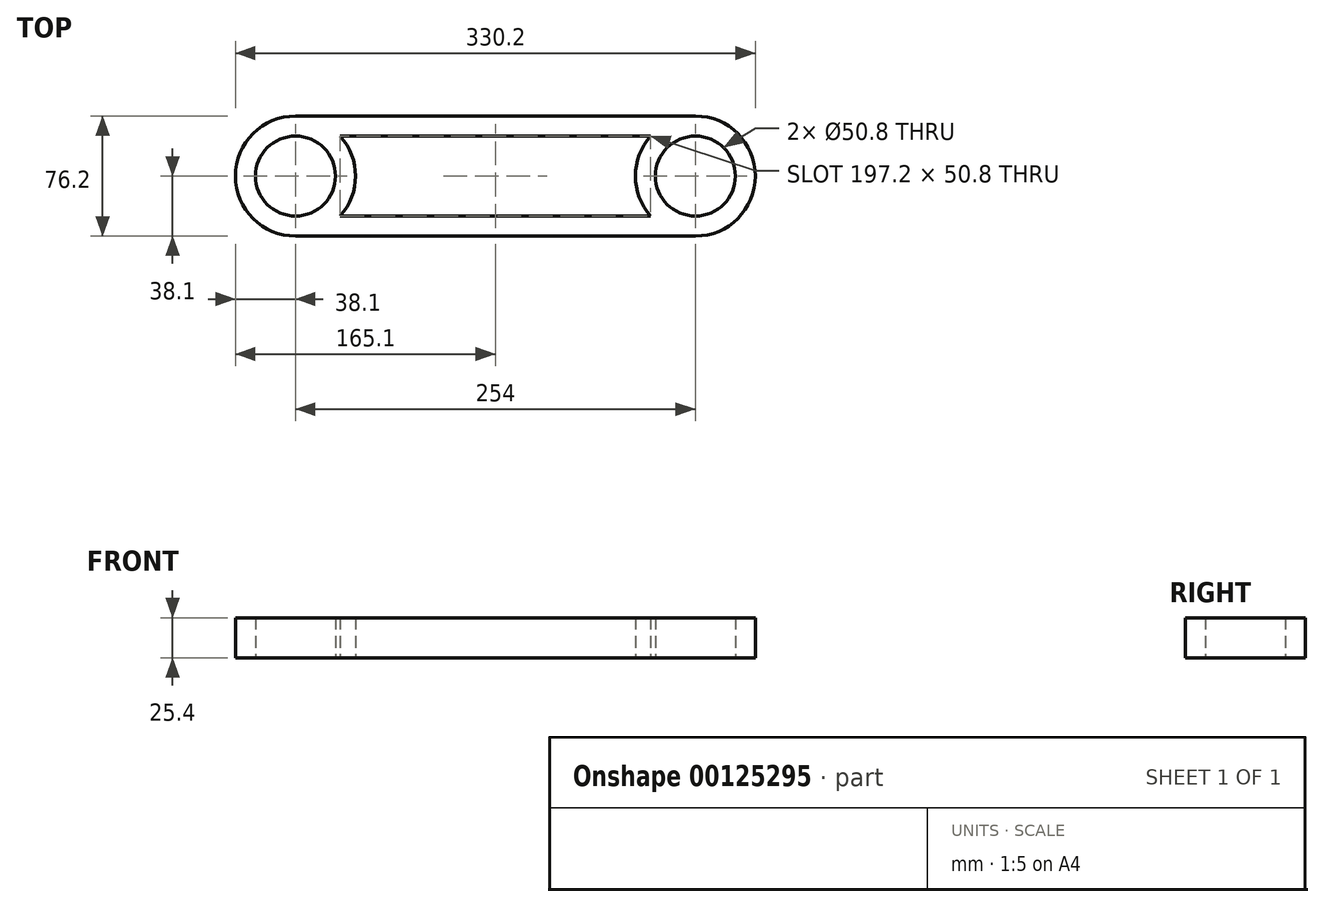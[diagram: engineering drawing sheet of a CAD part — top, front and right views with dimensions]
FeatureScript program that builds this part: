
annotation { "Feature Type Name" : "Feature", "Feature Type Description" : "" }
export const myFeature = defineFeature(function(context is Context, id is Id, definition is map)
    precondition{}
    {
        {
            var Q0;
            Q0=qCreatedBy(makeId("Top.planeOp"),FACE);
            var sketch = newSketch(context, id + "F0", { "sketchPlane" : qUnion([Q0])});
            skCircle(sketch, "E0", {"center": v(0, 0) * mm, "radius": 25.4 * mm});
            skCircle(sketch, "E1", {"center": v(0, 0) * mm, "radius": 38.1 * mm});
            skCircle(sketch, "E2", {"center": v(254, 0) * mm, "radius": 25.4 * mm});
            skCircle(sketch, "E3", {"center": v(254, 0) * mm, "radius": 38.1 * mm});
            skLineSegment(sketch, "E4", {"start": v(0, 38.1) * mm, "end": v(254, 38.1) * mm});
            skLineSegment(sketch, "E5", {"start": v(0, -25.4) * mm, "end": v(254, -25.4) * mm});
            skLineSegment(sketch, "E6", {"start": v(0, 25.4) * mm, "end": v(254, 25.4) * mm});
            skLineSegment(sketch, "E7", {"start": v(0, -38.1) * mm, "end": v(254, -38.1) * mm});
            skSolve(sketch);
        }
        {
            var Q0;
            {var subQ2=sQuery(id+"F0.wireOp",EDGE,"E5");var subQ7=sQuery(id+"F0.wireOp",EDGE,"E0");var subQ8=makeQuery(id+"F0.imprint","INTERSECT",VERTEX,{"derivedFrom":[subQ7,subQ2]});Q0=makeQuery(id+"F0.imprint","IMPRINT",FACE,{"disambiguationData":[TD([[makeQuery(id+"F0.imprint","IMPRINT",EDGE,{"disambiguationData":[TD([[subQ8,1.0]])],"derivedFrom":subQ7}),-1.0]])]});}
            var Q1;
            {var subQ0=sQuery(id+"F0.wireOp",EDGE,"E4");Q1=makeQuery(id+"F0.imprint","IMPRINT",FACE,{"disambiguationData":[TD([[makeQuery(id+"F0.imprint","IMPRINT",EDGE,{"derivedFrom":subQ0}),-1.0]])]});}
            var Q2;
            {var subQ3=sQuery(id+"F0.wireOp",EDGE,"E5");var subQ7=sQuery(id+"F0.wireOp",EDGE,"E2");var subQ8=makeQuery(id+"F0.imprint","INTERSECT",VERTEX,{"derivedFrom":[subQ7,subQ3]});Q2=makeQuery(id+"F0.imprint","IMPRINT",FACE,{"disambiguationData":[TD([[makeQuery(id+"F0.imprint","IMPRINT",EDGE,{"disambiguationData":[TD([[subQ8,-1.0]])],"derivedFrom":subQ7}),-1.0]])]});}
            var Q3;
            {var subQ0=sQuery(id+"F0.wireOp",EDGE,"E7");Q3=makeQuery(id+"F0.imprint","IMPRINT",FACE,{"disambiguationData":[TD([[makeQuery(id+"F0.imprint","IMPRINT",EDGE,{"derivedFrom":subQ0}),1.0]])]});}
            var Q4;
            {var subQ0=sQuery(id+"F0.wireOp",EDGE,"E5");var subQ1=sQuery(id+"F0.wireOp",EDGE,"E0");var subQ2=makeQuery(id+"F0.imprint","INTERSECT",VERTEX,{"derivedFrom":[subQ1,subQ0]});Q4=makeQuery(id+"F0.imprint","IMPRINT",FACE,{"disambiguationData":[TD([[makeQuery(id+"F0.imprint","IMPRINT",EDGE,{"disambiguationData":[TD([[subQ2,-1.0]])],"derivedFrom":subQ1}),-1.0]])]});}
            var Q5;
            {var subQ0=sQuery(id+"F0.wireOp",EDGE,"E5");var subQ1=sQuery(id+"F0.wireOp",EDGE,"E2");var subQ2=makeQuery(id+"F0.imprint","INTERSECT",VERTEX,{"derivedFrom":[subQ1,subQ0]});Q5=makeQuery(id+"F0.imprint","IMPRINT",FACE,{"disambiguationData":[TD([[makeQuery(id+"F0.imprint","IMPRINT",EDGE,{"disambiguationData":[TD([[subQ2,1.0]])],"derivedFrom":subQ1}),-1.0]])]});}
            extrude(context, id + "F1", {"entities" : qUnion([Q0, Q1, Q2, Q3, Q4, Q5]), "depth" : 25.4 * mm});
        }
    });
